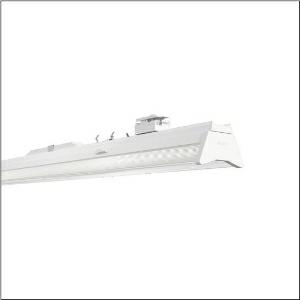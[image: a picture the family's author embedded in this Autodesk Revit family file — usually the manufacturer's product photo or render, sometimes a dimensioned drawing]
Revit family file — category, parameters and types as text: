
# Revit family: licross_21_performance_mo_52td16cn66xg
name_source: partatom
category: Lighting Fixtures
units: mm (PartAtom-declared; Revit-internal decimal feet)

## family parameters
Cut with Voids When Loaded = No
Host = Face
Light Source = No
Part Type = Normal
Room Calculation Point = No
Round Connector Dimension = Use Diameter
Shared = No

## types (1)
- --- (1 x LED, 5970 lm, 32.8 W, 6500K)
    Apparent Load = 33 VA
    CIE Flux Codes = 66 88 96 79 100
    Color Rendering = 80
    Color Temperature = 6500K
    Default Elevation = 1800 mm
    Description = Licross 21 Performance MO, luminaire insert, of sheet steel, galvanised, coil coated, white, length: 1.500mm, width: 120mm, height: 123mm, LED rated luminous flux: 5.970lm, light colour: 865, SDCM (Standard Deviation of Colour Matching)MacAdam ≤ 3 SDCM (initial), control gear: ON/OFF Multilumen, CLOi, with plug, 3-pole, with phase selection, mains connection: 220..240V, AC, 50/60Hz, start of lifetime: 33W, end of service life: 39W, internal wiring halogen-free, primary light control with lens, of plastic, primary optical cover: cover, of PMMA, light emission: direct/indirect distribution, primary light characteristic: symmetric, protection rating (complete): IP54, insulation class (complete): insulation class I (protective earthing), certification: CE, ENEC, UKCA, protection symbol: D if used in an environment with non-conductive dust loads with corresponding accessories, impact resistance: IK06, permissible ambient temperature for indoor applications: -35..+55°C, corresponds to IFS (International Featured Standards) requirements for safety and quality in the food industry, reducing of maximum allowable ambient temperature of 5°C with ceiling mounting, LABS conformity tested according to VDMA 24364:2018-05, The light source and the operating device comply with the requirements of the Ecodesign Regulation (EU) 2019/2020 and are replaceable in accordance with this regulation, packaging unit: 1 piece
    Height = 114 mm
    Lamp = 1 x LED
    Lamp Light Flux = 5970 lm
    Lamp Power = 32.8 W
    Lamp count = 1
    Length = 1500 mm
    Luminous efficacy = 182 lm/W
    Manufacturer = Siteco
    ModVariant = No
    Model = 52TD16CN66XG
    Mounting Place = Ceiling
    Mounting Type = Pendant
    Number of Poles = 1
    OnlyDefault = Yes
    Power Factor = 1
    Product Name = Licross 21 Performance MO
    Product group = luminaire insert | ceiling pendant
    ProductGroupID = 901
    Protection Class = Protection class I
    Protection Degree = IP 54
    RLX_Detail_Level = 1
    RLX_Emergency_Light_Flux = 0 lm
    RLX_Emergency_Type = 0
    RLX_Emergency_Type_DB = No
    RlxData = <blob elided: 32117 chars, md5=00faa6da>
    Socket = socket
    Standby Power = 0 W
    System Light Flux = 5970 lm
    System Power = 33 W
    Type Comments = factory setting: luminous flux: 100 % | (A | C | E) | 76 mA
    Type Image = l_1256138.jpg
    URL = http://relux.com
    VarID = @adj_056205
    Voltage = 0 V
    Weight = 0.00 kg
    Width = 120 mm

## geometry (parser evidence)
native form markers: Blend x4, Sweep x10
no freeform markers — native parametric forms only
